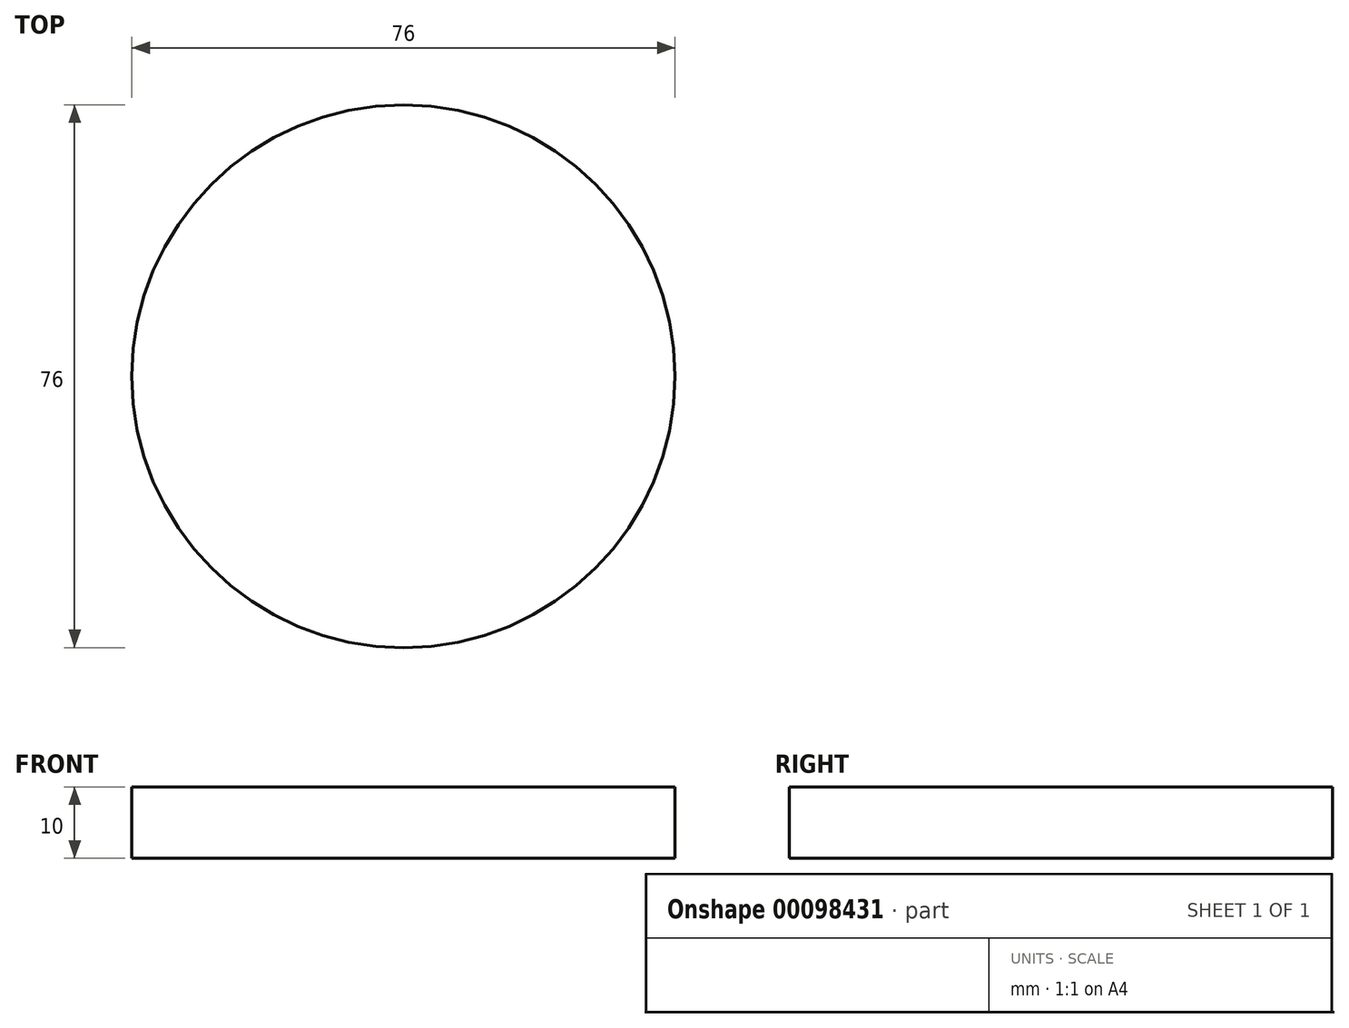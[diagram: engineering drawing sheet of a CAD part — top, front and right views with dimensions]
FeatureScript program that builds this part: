
annotation { "Feature Type Name" : "Feature", "Feature Type Description" : "" }
export const myFeature = defineFeature(function(context is Context, id is Id, definition is map)
    precondition{}
    {
        {
            var Q0;
            Q0=qCreatedBy(makeId("Top.planeOp"),FACE);
            var sketch = newSketch(context, id + "F0", { "sketchPlane" : qUnion([Q0])});
            skCircle(sketch, "E0", {"center": v(0, 0) * mm, "radius": 38 * mm});
            skSolve(sketch);
        }
        {
            var Q0;
            Q0 = qSketchRegion(id + "F0", true);
            extrude(context, id + "F1", {"entities" : qUnion([Q0]), "depth" : 10 * mm});
        }
    });
